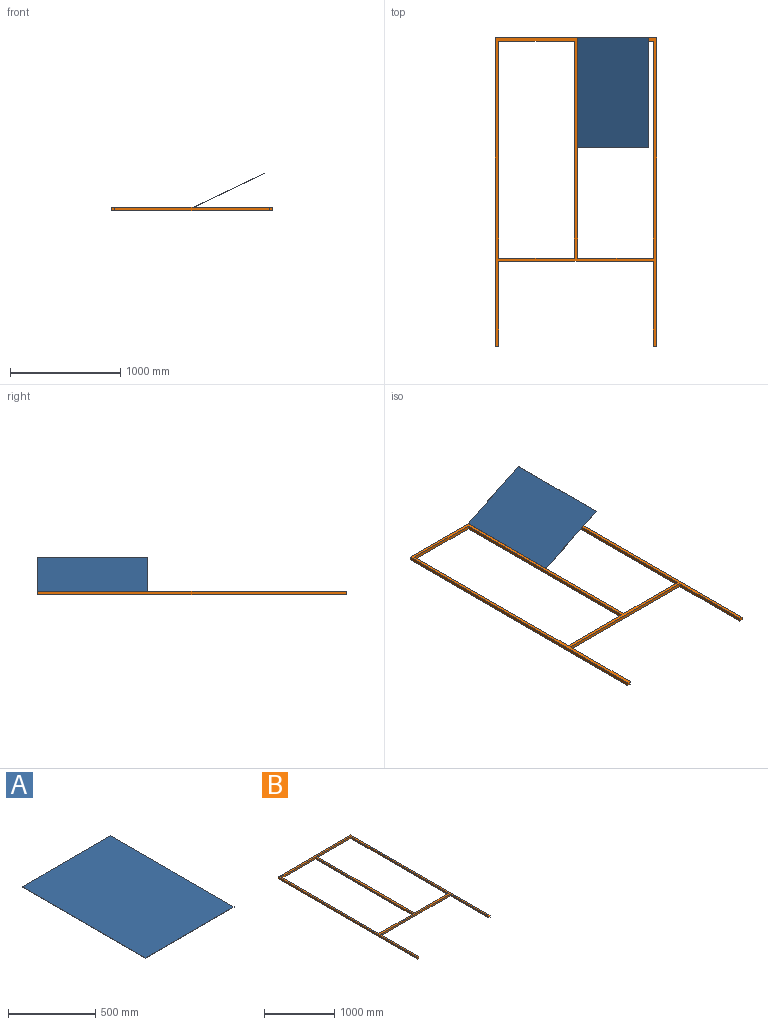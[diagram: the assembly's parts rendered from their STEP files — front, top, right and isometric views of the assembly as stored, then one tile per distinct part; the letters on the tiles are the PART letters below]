
ASSEMBLY  parts=2 mates=1
PART A: 6 faces, bbox 717.5x1000x2 mm
  f0: plane 1000x2mm, normal (1,0,0), area 2000mm2, adj f1,f3,f4,f5
  f1: plane 717.5x2mm, normal (0,1,0), area 1435mm2, adj f0,f2,f4,f5
  f2: plane 1000x2mm, normal (-1,0,0), area 2000mm2, adj f1,f3,f4,f5
  f3: plane 717.5x2mm, normal (0,-1,0), area 1435mm2, adj f0,f2,f4,f5
  f4: plane 1000x717.5mm, normal (0,0,1), area 717500mm2, adj f0,f1,f2,f3
  f5: plane 1000x717.5mm, normal (0,0,-1), area 717500mm2, adj f0,f1,f2,f3
PART B: 18 faces, bbox 1465x2800x30 mm
  f0: plane 1405x30mm, normal (0,-1,0), area 42150mm2, adj f1,f15,f16,f17
  f1: plane 770x30mm, normal (-1,0,0), area 23100mm2, adj f0,f2,f16,f17
  f2: plane 30x30mm, normal (0,-1,0), area 900mm2, adj f1,f3,f16,f17
  f3: plane 2800x30mm, normal (1,0,0), area 84000mm2, adj f2,f4,f16,f17
  f4: plane 1465x30mm, normal (0,1,0), area 43950mm2, adj f3,f5,f16,f17
  f5: plane 2800x30mm, normal (-1,0,0), area 84000mm2, adj f4,f6,f16,f17
  f6: plane 30x30mm, normal (0,-1,0), area 900mm2, adj f5,f15,f16,f17
  f7: plane 687.5x30mm, normal (0,-1,0), area 20625mm2, adj f8,f13,f16,f17
  f8: plane 1970x30mm, normal (-1,0,0), area 59100mm2, adj f7,f9,f16,f17
  f9: plane 687.5x30mm, normal (0,1,0), area 20625mm2, adj f8,f13,f16,f17
  f10: plane 687.5x30mm, normal (0,1,0), area 20625mm2, adj f11,f14,f16,f17
  f11: plane 1970x30mm, normal (1,0,0), area 59100mm2, adj f10,f12,f16,f17
  f12: plane 687.5x30mm, normal (0,-1,0), area 20625mm2, adj f11,f14,f16,f17
  f13: plane 1970x30mm, normal (1,0,0), area 59100mm2, adj f7,f9,f16,f17
  f14: plane 1970x30mm, normal (-1,0,0), area 59100mm2, adj f10,f12,f16,f17
  f15: plane 770x30mm, normal (1,0,0), area 23100mm2, adj f0,f6,f16,f17
  f16: plane 2800x1465mm, normal (0,0,1), area 311400mm2, adj f0,f1,f2,f3,f4,f5,f6,f7
  f17: plane 2800x1465mm, normal (0,0,-1), area 311400mm2, adj f0,f1,f2,f3,f4,f5,f6,f7
PLACE A rot(axis=(0,-1,0),25.6deg) t=(336.43,891.1,160.21)mm
PLACE B t=(-2.78,-8.22,-24.91)mm fixed
MATE revolute A.f1 <-> B.f4  axis (0,-1,0) through (12.22,1391.78,5.09)mm
